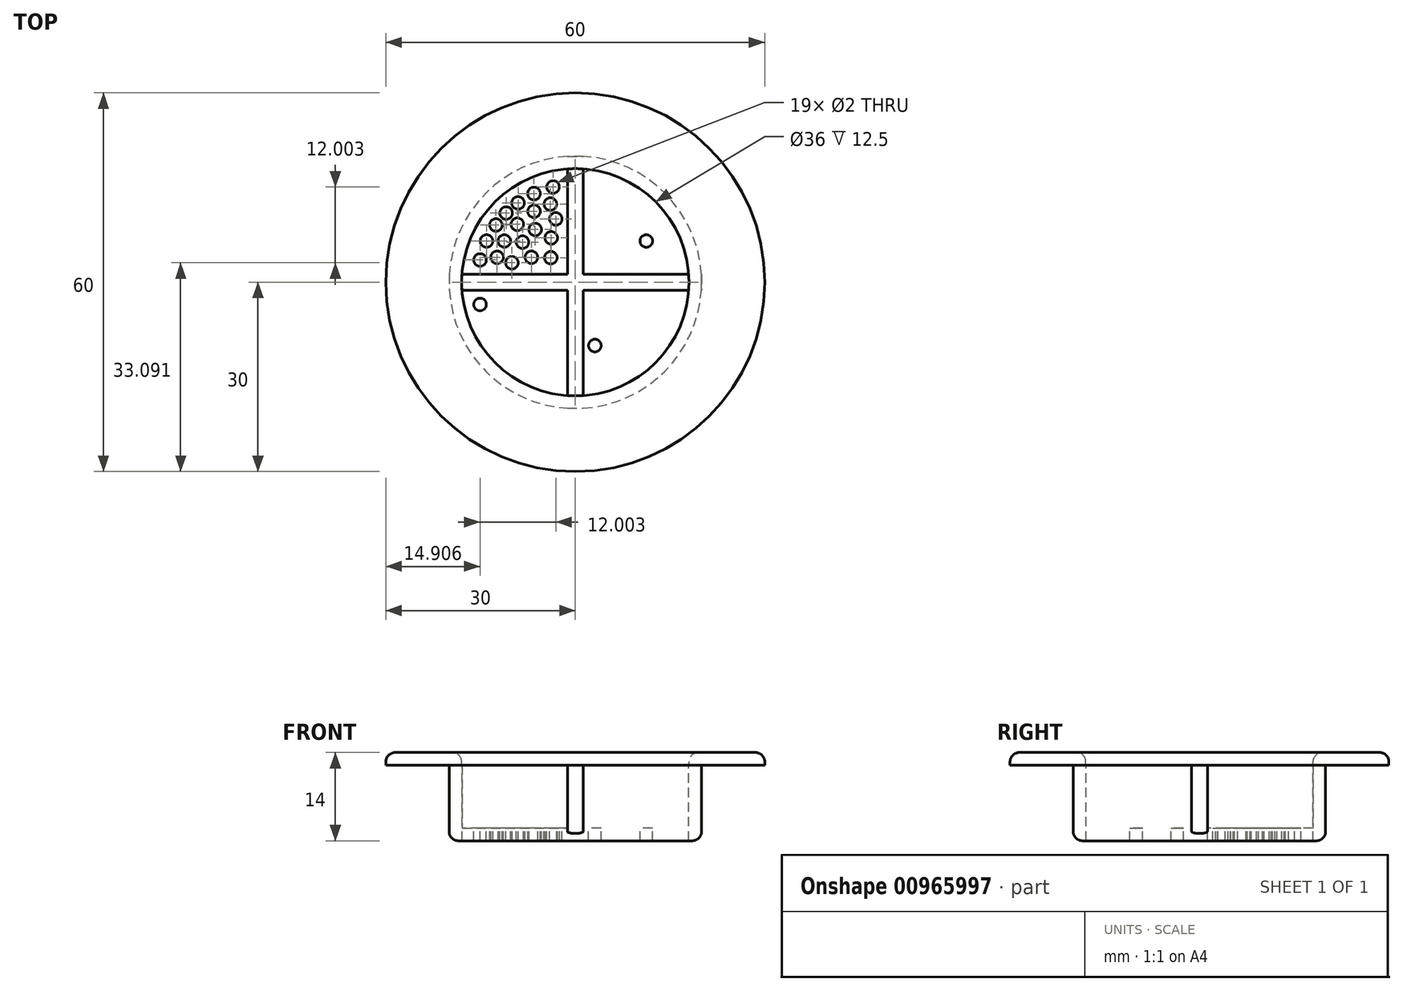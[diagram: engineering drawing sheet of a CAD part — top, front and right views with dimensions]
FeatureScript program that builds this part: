
annotation { "Feature Type Name" : "Feature", "Feature Type Description" : "" }
export const myFeature = defineFeature(function(context is Context, id is Id, definition is map)
    precondition{}
    {
        {
            var Q0;
            Q0=qCreatedBy(makeId("Top.planeOp"),FACE);
            var sketch = newSketch(context, id + "F0", { "sketchPlane" : qUnion([Q0])});
            skCircle(sketch, "E0", {"center": v(0, 0) * mm, "radius": 20 * mm});
            skCircle(sketch, "E1", {"center": v(0, 0) * mm, "radius": 18 * mm});
            skLineSegment(sketch, "E2.bottom", {"start": v(-1.25, 19.96) * mm, "end": v(1.25, 19.96) * mm});
            skLineSegment(sketch, "E2.top", {"start": v(-1.25, -19.96) * mm, "end": v(1.25, -19.96) * mm});
            skLineSegment(sketch, "E2.left", {"start": v(-1.25, 19.96) * mm, "end": v(-1.25, -19.96) * mm});
            skLineSegment(sketch, "E2.right", {"start": v(1.25, 19.96) * mm, "end": v(1.25, -19.96) * mm});
            skLineSegment(sketch, "E3.bottom", {"start": v(-19.96, 1.25) * mm, "end": v(19.96, 1.25) * mm});
            skLineSegment(sketch, "E3.top", {"start": v(-19.96, -1.25) * mm, "end": v(19.96, -1.25) * mm});
            skLineSegment(sketch, "E3.left", {"start": v(-19.96, 1.25) * mm, "end": v(-19.96, -1.25) * mm});
            skLineSegment(sketch, "E3.right", {"start": v(19.96, 1.25) * mm, "end": v(19.96, -1.25) * mm});
            skCircle(sketch, "E4", {"center": v(0, 0) * mm, "radius": 5.5 * mm, "construction": true});
            skCircle(sketch, "E5", {"center": v(0, 0) * mm, "radius": 8 * mm, "construction": true});
            skCircle(sketch, "E6", {"center": v(0, 0) * mm, "radius": 10.5 * mm, "construction": true});
            skCircle(sketch, "E7", {"center": v(0, 0) * mm, "radius": 13 * mm, "construction": true});
            skCircle(sketch, "E8", {"center": v(0, 0) * mm, "radius": 15.5 * mm, "construction": true});
            skLineSegment(sketch, "E9", {"start": v(0, 0) * mm, "end": v(-18.69, 18.69) * mm, "construction": true});
            skCircle(sketch, "E10", {"center": v(-3.89, 3.89) * mm, "radius": 1 * mm});
            skCircle(sketch, "E11", {"center": v(-10.96, 10.96) * mm, "radius": 1 * mm});
            skCircle(sketch, "E12", {"center": v(-6.95, 3.96) * mm, "radius": 1 * mm});
            skCircle(sketch, "E13", {"center": v(-3.81, 7.03) * mm, "radius": 1 * mm});
            skCircle(sketch, "E14", {"center": v(-12.38, 3.96) * mm, "radius": 1 * mm});
            skCircle(sketch, "E15", {"center": v(-15.1, 3.52) * mm, "radius": 1 * mm});
            skCircle(sketch, "E16", {"center": v(-10.03, 3.1) * mm, "radius": 1 * mm});
            skCircle(sketch, "E17", {"center": v(-14.06, 6.53) * mm, "radius": 1 * mm});
            skCircle(sketch, "E18", {"center": v(-11.24, 6.53) * mm, "radius": 1 * mm});
            skCircle(sketch, "E19", {"center": v(-12.57, 9.07) * mm, "radius": 1 * mm});
            skCircle(sketch, "E20", {"center": v(-9.2, 9.2) * mm, "radius": 1 * mm});
            skCircle(sketch, "E21", {"center": v(-8.36, 6.35) * mm, "radius": 1 * mm});
            skCircle(sketch, "E22.MirrorC", {"center": v(-9.07, 12.57) * mm, "radius": 1 * mm});
            skCircle(sketch, "E23.MirrorC", {"center": v(-6.53, 14.06) * mm, "radius": 1 * mm});
            skCircle(sketch, "E24.MirrorC", {"center": v(-3.52, 15.1) * mm, "radius": 1 * mm});
            skCircle(sketch, "E25.MirrorC", {"center": v(-3.96, 12.38) * mm, "radius": 1 * mm});
            skCircle(sketch, "E26.MirrorC", {"center": v(-6.53, 11.24) * mm, "radius": 1 * mm});
            skCircle(sketch, "E27.MirrorC", {"center": v(-3.1, 10.03) * mm, "radius": 1 * mm});
            skCircle(sketch, "E28.MirrorC", {"center": v(-6.35, 8.36) * mm, "radius": 1 * mm});
            skCircle(sketch, "E29.MirrorC", {"center": v(-15.1, -3.52) * mm, "radius": 1 * mm});
            skCircle(sketch, "E30.MirrorC", {"center": v(-12.38, -3.96) * mm, "radius": 1 * mm});
            skCircle(sketch, "E31.MirrorC", {"center": v(-10.03, -3.1) * mm, "radius": 1 * mm});
            skCircle(sketch, "E32.MirrorC", {"center": v(-3.89, -3.89) * mm, "radius": 1 * mm});
            skCircle(sketch, "E33.MirrorC", {"center": v(-3.81, -7.03) * mm, "radius": 1 * mm});
            skCircle(sketch, "E34.MirrorC", {"center": v(-8.36, -6.35) * mm, "radius": 1 * mm});
            skCircle(sketch, "E35.MirrorC", {"center": v(-11.24, -6.53) * mm, "radius": 1 * mm});
            skCircle(sketch, "E36.MirrorC", {"center": v(-14.06, -6.53) * mm, "radius": 1 * mm});
            skCircle(sketch, "E37.MirrorC", {"center": v(-12.57, -9.07) * mm, "radius": 1 * mm});
            skCircle(sketch, "E38.MirrorC", {"center": v(-9.2, -9.2) * mm, "radius": 1 * mm});
            skCircle(sketch, "E39.MirrorC", {"center": v(-10.96, -10.96) * mm, "radius": 1 * mm});
            skCircle(sketch, "E40.MirrorC", {"center": v(-6.35, -8.36) * mm, "radius": 1 * mm});
            skCircle(sketch, "E41.MirrorC", {"center": v(-3.1, -10.03) * mm, "radius": 1 * mm});
            skCircle(sketch, "E42.MirrorC", {"center": v(-3.96, -12.38) * mm, "radius": 1 * mm});
            skCircle(sketch, "E43.MirrorC", {"center": v(-6.53, -11.24) * mm, "radius": 1 * mm});
            skCircle(sketch, "E44.MirrorC", {"center": v(-6.53, -14.06) * mm, "radius": 1 * mm});
            skCircle(sketch, "E45.MirrorC", {"center": v(-9.07, -12.57) * mm, "radius": 1 * mm});
            skCircle(sketch, "E46.MirrorC", {"center": v(-3.52, -15.1) * mm, "radius": 1 * mm});
            skCircle(sketch, "E47.MirrorC", {"center": v(-6.95, -3.96) * mm, "radius": 1 * mm});
            skCircle(sketch, "E48.MirrorC", {"center": v(11.24, 6.53) * mm, "radius": 1 * mm});
            skCircle(sketch, "E49.MirrorC", {"center": v(14.06, 6.53) * mm, "radius": 1 * mm});
            skCircle(sketch, "E50.MirrorC", {"center": v(8.36, 6.35) * mm, "radius": 1 * mm});
            skCircle(sketch, "E51.MirrorC", {"center": v(3.81, 7.03) * mm, "radius": 1 * mm});
            skCircle(sketch, "E52.MirrorC", {"center": v(15.1, 3.52) * mm, "radius": 1 * mm});
            skCircle(sketch, "E53.MirrorC", {"center": v(3.89, 3.89) * mm, "radius": 1 * mm});
            skCircle(sketch, "E54.MirrorC", {"center": v(10.03, 3.1) * mm, "radius": 1 * mm});
            skCircle(sketch, "E55.MirrorC", {"center": v(6.95, 3.96) * mm, "radius": 1 * mm});
            skCircle(sketch, "E56.MirrorC", {"center": v(12.38, 3.96) * mm, "radius": 1 * mm});
            skCircle(sketch, "E57.MirrorC", {"center": v(6.53, 14.06) * mm, "radius": 1 * mm});
            skCircle(sketch, "E58.MirrorC", {"center": v(9.07, 12.57) * mm, "radius": 1 * mm});
            skCircle(sketch, "E59.MirrorC", {"center": v(10.96, 10.96) * mm, "radius": 1 * mm});
            skCircle(sketch, "E60.MirrorC", {"center": v(9.2, 9.2) * mm, "radius": 1 * mm});
            skCircle(sketch, "E61.MirrorC", {"center": v(6.53, 11.24) * mm, "radius": 1 * mm});
            skCircle(sketch, "E62.MirrorC", {"center": v(3.52, 15.1) * mm, "radius": 1 * mm});
            skCircle(sketch, "E63.MirrorC", {"center": v(12.57, 9.07) * mm, "radius": 1 * mm});
            skCircle(sketch, "E64.MirrorC", {"center": v(3.1, 10.03) * mm, "radius": 1 * mm});
            skCircle(sketch, "E65.MirrorC", {"center": v(6.35, 8.36) * mm, "radius": 1 * mm});
            skCircle(sketch, "E66.MirrorC", {"center": v(3.96, 12.38) * mm, "radius": 1 * mm});
            skCircle(sketch, "E67.MirrorC", {"center": v(3.81, -7.03) * mm, "radius": 1 * mm});
            skCircle(sketch, "E68.MirrorC", {"center": v(3.1, -10.03) * mm, "radius": 1 * mm});
            skCircle(sketch, "E69.MirrorC", {"center": v(6.53, -11.24) * mm, "radius": 1 * mm});
            skCircle(sketch, "E70.MirrorC", {"center": v(12.38, -3.96) * mm, "radius": 1 * mm});
            skCircle(sketch, "E71.MirrorC", {"center": v(15.1, -3.52) * mm, "radius": 1 * mm});
            skCircle(sketch, "E72.MirrorC", {"center": v(9.2, -9.2) * mm, "radius": 1 * mm});
            skCircle(sketch, "E73.MirrorC", {"center": v(8.36, -6.35) * mm, "radius": 1 * mm});
            skCircle(sketch, "E74.MirrorC", {"center": v(14.06, -6.53) * mm, "radius": 1 * mm});
            skCircle(sketch, "E75.MirrorC", {"center": v(3.89, -3.89) * mm, "radius": 1 * mm});
            skCircle(sketch, "E76.MirrorC", {"center": v(11.24, -6.53) * mm, "radius": 1 * mm});
            skCircle(sketch, "E77.MirrorC", {"center": v(6.35, -8.36) * mm, "radius": 1 * mm});
            skCircle(sketch, "E78.MirrorC", {"center": v(9.07, -12.57) * mm, "radius": 1 * mm});
            skCircle(sketch, "E79.MirrorC", {"center": v(3.96, -12.38) * mm, "radius": 1 * mm});
            skCircle(sketch, "E80.MirrorC", {"center": v(10.96, -10.96) * mm, "radius": 1 * mm});
            skCircle(sketch, "E81.MirrorC", {"center": v(6.53, -14.06) * mm, "radius": 1 * mm});
            skCircle(sketch, "E82.MirrorC", {"center": v(3.52, -15.1) * mm, "radius": 1 * mm});
            skCircle(sketch, "E83.MirrorC", {"center": v(10.03, -3.1) * mm, "radius": 1 * mm});
            skCircle(sketch, "E84.MirrorC", {"center": v(12.57, -9.07) * mm, "radius": 1 * mm});
            skCircle(sketch, "E85.MirrorC", {"center": v(6.95, -3.96) * mm, "radius": 1 * mm});
            skSolve(sketch);
        }
        {
            var Q0;
            {var subQ0=sQuery(id+"F0.wireOp",EDGE,"E2.left");var subQ5=sQuery(id+"F0.wireOp",EDGE,"E1");var subQ6=makeQuery(id+"F0.imprint","INTERSECT",VERTEX,{"disambiguationData":[OD(0.0)],"derivedFrom":[subQ5,subQ0]});Q0=makeQuery(id+"F0.imprint","IMPRINT",FACE,{"disambiguationData":[TD([[makeQuery(id+"F0.imprint","IMPRINT",EDGE,{"disambiguationData":[TD([[subQ6,-1.0]])],"derivedFrom":subQ5}),-1.0]])]});}
            var Q1;
            Q1=makeQuery(id+"F0.imprint","IMPRINT",FACE,{"disambiguationData":[TD([[makeQuery(id+"F0.imprint","IMPRINT",EDGE,{"derivedFrom":sQuery(id+"F0.wireOp",EDGE,"E10")}),-1.0]])]});
            var Q2;
            {var subQ5=sQuery(id+"F0.wireOp",EDGE,"E3.left");Q2=makeQuery(id+"F0.imprint","IMPRINT",FACE,{"disambiguationData":[TD([[makeQuery(id+"F0.imprint","IMPRINT",EDGE,{"derivedFrom":subQ5}),1.0]])]});}
            var Q3;
            {var subQ0=sQuery(id+"F0.wireOp",EDGE,"E3.bottom");var subQ1=sQuery(id+"F0.wireOp",EDGE,"E1");var subQ2=makeQuery(id+"F0.imprint","INTERSECT",VERTEX,{"disambiguationData":[OD(1.0)],"derivedFrom":[subQ1,subQ0]});Q3=makeQuery(id+"F0.imprint","IMPRINT",FACE,{"disambiguationData":[TD([[makeQuery(id+"F0.imprint","IMPRINT",EDGE,{"disambiguationData":[TD([[subQ2,-1.0]])],"derivedFrom":subQ1}),1.0]])]});}
            var Q4;
            {var subQ3=sQuery(id+"F0.wireOp",EDGE,"E3.top");var subQ5=sQuery(id+"F0.wireOp",EDGE,"E1");var subQ6=makeQuery(id+"F0.imprint","INTERSECT",VERTEX,{"disambiguationData":[OD(0.0)],"derivedFrom":[subQ5,subQ3]});Q4=makeQuery(id+"F0.imprint","IMPRINT",FACE,{"disambiguationData":[TD([[makeQuery(id+"F0.imprint","IMPRINT",EDGE,{"disambiguationData":[TD([[subQ6,-1.0]])],"derivedFrom":subQ5}),-1.0]])]});}
            var Q5;
            Q5=makeQuery(id+"F0.imprint","IMPRINT",FACE,{"disambiguationData":[TD([[makeQuery(id+"F0.imprint","IMPRINT",EDGE,{"derivedFrom":sQuery(id+"F0.wireOp",EDGE,"E29.MirrorC")}),1.0]])]});
            var Q6;
            {var subQ5=sQuery(id+"F0.wireOp",EDGE,"E2.top");Q6=makeQuery(id+"F0.imprint","IMPRINT",FACE,{"disambiguationData":[TD([[makeQuery(id+"F0.imprint","IMPRINT",EDGE,{"derivedFrom":subQ5}),1.0]])]});}
            var Q7;
            {var subQ0=sQuery(id+"F0.wireOp",EDGE,"E2.left");var subQ1=sQuery(id+"F0.wireOp",EDGE,"E1");var subQ2=makeQuery(id+"F0.imprint","INTERSECT",VERTEX,{"disambiguationData":[OD(1.0)],"derivedFrom":[subQ1,subQ0]});Q7=makeQuery(id+"F0.imprint","IMPRINT",FACE,{"disambiguationData":[TD([[makeQuery(id+"F0.imprint","IMPRINT",EDGE,{"disambiguationData":[TD([[subQ2,-1.0]])],"derivedFrom":subQ1}),1.0]])]});}
            var Q8;
            {var subQ0=sQuery(id+"F0.wireOp",EDGE,"E3.bottom");var subQ1=sQuery(id+"F0.wireOp",EDGE,"E2.left");var subQ2=makeQuery(id+"F0.imprint","INTERSECT",VERTEX,{"derivedFrom":[subQ1,subQ0]});Q8=makeQuery(id+"F0.imprint","IMPRINT",FACE,{"disambiguationData":[TD([[makeQuery(id+"F0.imprint","IMPRINT",EDGE,{"disambiguationData":[TD([[subQ2,-1.0]])],"derivedFrom":subQ1}),1.0]])]});}
            var Q9;
            {var subQ0=sQuery(id+"F0.wireOp",EDGE,"E2.right");var subQ1=sQuery(id+"F0.wireOp",EDGE,"E1");var subQ2=makeQuery(id+"F0.imprint","INTERSECT",VERTEX,{"disambiguationData":[OD(0.0)],"derivedFrom":[subQ1,subQ0]});Q9=makeQuery(id+"F0.imprint","IMPRINT",FACE,{"disambiguationData":[TD([[makeQuery(id+"F0.imprint","IMPRINT",EDGE,{"disambiguationData":[TD([[subQ2,-1.0]])],"derivedFrom":subQ1}),1.0]])]});}
            var Q10;
            {var subQ5=sQuery(id+"F0.wireOp",EDGE,"E2.bottom");Q10=makeQuery(id+"F0.imprint","IMPRINT",FACE,{"disambiguationData":[TD([[makeQuery(id+"F0.imprint","IMPRINT",EDGE,{"derivedFrom":subQ5}),-1.0]])]});}
            var Q11;
            {var subQ0=sQuery(id+"F0.wireOp",EDGE,"E2.right");var subQ5=sQuery(id+"F0.wireOp",EDGE,"E1");var subQ6=makeQuery(id+"F0.imprint","INTERSECT",VERTEX,{"disambiguationData":[OD(0.0)],"derivedFrom":[subQ5,subQ0]});Q11=makeQuery(id+"F0.imprint","IMPRINT",FACE,{"disambiguationData":[TD([[makeQuery(id+"F0.imprint","IMPRINT",EDGE,{"disambiguationData":[TD([[subQ6,1.0]])],"derivedFrom":subQ5}),-1.0]])]});}
            var Q12;
            Q12=makeQuery(id+"F0.imprint","IMPRINT",FACE,{"disambiguationData":[TD([[makeQuery(id+"F0.imprint","IMPRINT",EDGE,{"derivedFrom":sQuery(id+"F0.wireOp",EDGE,"E48.MirrorC")}),1.0]])]});
            var Q13;
            {var subQ5=sQuery(id+"F0.wireOp",EDGE,"E3.right");Q13=makeQuery(id+"F0.imprint","IMPRINT",FACE,{"disambiguationData":[TD([[makeQuery(id+"F0.imprint","IMPRINT",EDGE,{"derivedFrom":subQ5}),-1.0]])]});}
            var Q14;
            {var subQ0=sQuery(id+"F0.wireOp",EDGE,"E3.bottom");var subQ1=sQuery(id+"F0.wireOp",EDGE,"E1");var subQ2=makeQuery(id+"F0.imprint","INTERSECT",VERTEX,{"disambiguationData":[OD(0.0)],"derivedFrom":[subQ1,subQ0]});Q14=makeQuery(id+"F0.imprint","IMPRINT",FACE,{"disambiguationData":[TD([[makeQuery(id+"F0.imprint","IMPRINT",EDGE,{"disambiguationData":[TD([[subQ2,1.0]])],"derivedFrom":subQ1}),1.0]])]});}
            var Q15;
            {var subQ0=sQuery(id+"F0.wireOp",EDGE,"E2.right");var subQ5=sQuery(id+"F0.wireOp",EDGE,"E1");var subQ6=makeQuery(id+"F0.imprint","INTERSECT",VERTEX,{"disambiguationData":[OD(1.0)],"derivedFrom":[subQ5,subQ0]});Q15=makeQuery(id+"F0.imprint","IMPRINT",FACE,{"disambiguationData":[TD([[makeQuery(id+"F0.imprint","IMPRINT",EDGE,{"disambiguationData":[TD([[subQ6,-1.0]])],"derivedFrom":subQ5}),-1.0]])]});}
            var Q16;
            Q16=makeQuery(id+"F0.imprint","IMPRINT",FACE,{"disambiguationData":[TD([[makeQuery(id+"F0.imprint","IMPRINT",EDGE,{"derivedFrom":sQuery(id+"F0.wireOp",EDGE,"E68.MirrorC")}),1.0]])]});
            extrude(context, id + "F1", {"entities" : qUnion([Q0, Q1, Q2, Q3, Q4, Q5, Q6, Q7, Q8, Q9, Q10, Q11, Q12, Q13, Q14, Q15, Q16]), "oppositeDirection" : true, "depth" : 2 * mm, "offsetDistance" : 25 * mm});
        }
        {
            var Q0;
            {var subQ0=sQuery(id+"F0.wireOp",EDGE,"E2.left");var subQ5=sQuery(id+"F0.wireOp",EDGE,"E1");var subQ6=makeQuery(id+"F0.imprint","INTERSECT",VERTEX,{"disambiguationData":[OD(0.0)],"derivedFrom":[subQ5,subQ0]});Q0=makeQuery(id+"F0.imprint","IMPRINT",FACE,{"disambiguationData":[TD([[makeQuery(id+"F0.imprint","IMPRINT",EDGE,{"disambiguationData":[TD([[subQ6,-1.0]])],"derivedFrom":subQ5}),-1.0]])]});}
            var Q1;
            {var subQ5=sQuery(id+"F0.wireOp",EDGE,"E3.left");Q1=makeQuery(id+"F0.imprint","IMPRINT",FACE,{"disambiguationData":[TD([[makeQuery(id+"F0.imprint","IMPRINT",EDGE,{"derivedFrom":subQ5}),1.0]])]});}
            var Q2;
            {var subQ5=sQuery(id+"F0.wireOp",EDGE,"E2.bottom");Q2=makeQuery(id+"F0.imprint","IMPRINT",FACE,{"disambiguationData":[TD([[makeQuery(id+"F0.imprint","IMPRINT",EDGE,{"derivedFrom":subQ5}),-1.0]])]});}
            var Q3;
            {var subQ0=sQuery(id+"F0.wireOp",EDGE,"E2.right");var subQ5=sQuery(id+"F0.wireOp",EDGE,"E1");var subQ6=makeQuery(id+"F0.imprint","INTERSECT",VERTEX,{"disambiguationData":[OD(0.0)],"derivedFrom":[subQ5,subQ0]});Q3=makeQuery(id+"F0.imprint","IMPRINT",FACE,{"disambiguationData":[TD([[makeQuery(id+"F0.imprint","IMPRINT",EDGE,{"disambiguationData":[TD([[subQ6,1.0]])],"derivedFrom":subQ5}),-1.0]])]});}
            var Q4;
            {var subQ5=sQuery(id+"F0.wireOp",EDGE,"E3.right");Q4=makeQuery(id+"F0.imprint","IMPRINT",FACE,{"disambiguationData":[TD([[makeQuery(id+"F0.imprint","IMPRINT",EDGE,{"derivedFrom":subQ5}),-1.0]])]});}
            var Q5;
            {var subQ0=sQuery(id+"F0.wireOp",EDGE,"E2.right");var subQ5=sQuery(id+"F0.wireOp",EDGE,"E1");var subQ6=makeQuery(id+"F0.imprint","INTERSECT",VERTEX,{"disambiguationData":[OD(1.0)],"derivedFrom":[subQ5,subQ0]});Q5=makeQuery(id+"F0.imprint","IMPRINT",FACE,{"disambiguationData":[TD([[makeQuery(id+"F0.imprint","IMPRINT",EDGE,{"disambiguationData":[TD([[subQ6,-1.0]])],"derivedFrom":subQ5}),-1.0]])]});}
            var Q6;
            {var subQ5=sQuery(id+"F0.wireOp",EDGE,"E2.top");Q6=makeQuery(id+"F0.imprint","IMPRINT",FACE,{"disambiguationData":[TD([[makeQuery(id+"F0.imprint","IMPRINT",EDGE,{"derivedFrom":subQ5}),1.0]])]});}
            var Q7;
            {var subQ3=sQuery(id+"F0.wireOp",EDGE,"E3.top");var subQ5=sQuery(id+"F0.wireOp",EDGE,"E1");var subQ6=makeQuery(id+"F0.imprint","INTERSECT",VERTEX,{"disambiguationData":[OD(0.0)],"derivedFrom":[subQ5,subQ3]});Q7=makeQuery(id+"F0.imprint","IMPRINT",FACE,{"disambiguationData":[TD([[makeQuery(id+"F0.imprint","IMPRINT",EDGE,{"disambiguationData":[TD([[subQ6,-1.0]])],"derivedFrom":subQ5}),-1.0]])]});}
            extrude(context, id + "F2", {"entities" : qUnion([Q0, Q1, Q2, Q3, Q4, Q5, Q6, Q7]), "operationType" : NewBodyOperationType.ADD, "depth" : 10 * mm, "offsetDistance" : 25 * mm});
        }
        {
            var Q0;
            Q0=makeQuery(id+"F2.opExtrude","CAP_EDGE",EDGE,{"disambiguationData":[OSD([sQuery(id+"F0.wireOp",EDGE,"E1")])],"isStart":true});
            var Q1;
            {var subQ0=sQuery(id+"F0.wireOp",EDGE,"E0");Q1=makeQuery(id+"F1.opExtrude","CAP_EDGE",EDGE,{"disambiguationData":[OSD([subQ0]),TDD([makeQuery(id+"F0.imprint","IMPRINT",EDGE,{"disambiguationData":[TD([[makeQuery(id+"F0.imprint","INTERSECT",VERTEX,{"derivedFrom":[subQ0,sQuery(id+"F0.wireOp",EDGE,"E2.bottom"),sQuery(id+"F0.wireOp",EDGE,"E2.left")]}),-1.0]])],"derivedFrom":subQ0})])],"isStart":false});}
            fillet(context, id + "F3", {"entities" : qUnion([Q0, Q1]), "radius" : 1.5 * mm, "tangentPropagation" : true, "allowEdgeOverflow" : false});
        }
        {
            var Q0;
            Q0=makeQuery(id+"F2.opExtrude","CAP_FACE",FACE,{"disambiguationData":[OSD([sQuery(id+"F0.wireOp",EDGE,"E0"),sQuery(id+"F0.wireOp",EDGE,"E1"),sQuery(id+"F0.wireOp",EDGE,"E2.bottom"),sQuery(id+"F0.wireOp",EDGE,"E2.top"),sQuery(id+"F0.wireOp",EDGE,"E3.left"),sQuery(id+"F0.wireOp",EDGE,"E3.right")])],"isStart":false});
            var sketch = newSketch(context, id + "F4", { "sketchPlane" : qUnion([Q0])});
            skCircle(sketch, "E86.0", {"center": v(0, 0) * mm, "radius": 18 * mm});
            skCircle(sketch, "E87.0", {"center": v(0, 0) * mm, "radius": 30 * mm});
            skSolve(sketch);
        }
        {
            var Q0;
            Q0=makeQuery(id+"F4.imprint","IMPRINT",FACE,{"disambiguationData":[TD([[makeQuery(id+"F4.imprint","IMPRINT",EDGE,{"derivedFrom":sQuery(id+"F4.wireOp",EDGE,"E87.0")}),1.0]])]});
            var Q1;
            Q1=makeQuery(id+"F4.imprint","IMPRINT",FACE,{"disambiguationData":[TD([[makeQuery(id+"F4.imprint","IMPRINT",EDGE,{"derivedFrom":sQuery(id+"F4.wireOp",EDGE,"E86.0")}),-1.0]])]});
            extrude(context, id + "F5", {"entities" : qUnion([Q0, Q1]), "operationType" : NewBodyOperationType.ADD, "depth" : 2 * mm, "offsetDistance" : 25 * mm});
        }
        {
            var Q0;
            Q0=makeQuery(id+"F5.opExtrude","CAP_EDGE",EDGE,{"disambiguationData":[OSD([sQuery(id+"F4.wireOp",EDGE,"E87.0")])],"isStart":false});
            var Q1;
            Q1=makeQuery(id+"F5.opExtrude","CAP_EDGE",EDGE,{"disambiguationData":[OSD([sQuery(id+"F4.wireOp",EDGE,"E86.0")])],"isStart":false});
            fillet(context, id + "F6", {"entities" : qUnion([Q0, Q1]), "radius" : 1.5 * mm, "tangentPropagation" : true, "allowEdgeOverflow" : false});
        }
        {
            var Q0;
            {var subQ0=sQuery(id+"F0.wireOp",EDGE,"E2.left");var subQ1=sQuery(id+"F0.wireOp",EDGE,"E1");var subQ2=makeQuery(id+"F0.imprint","INTERSECT",VERTEX,{"disambiguationData":[OD(1.0)],"derivedFrom":[subQ1,subQ0]});Q0=makeQuery(id+"F0.imprint","IMPRINT",FACE,{"disambiguationData":[TD([[makeQuery(id+"F0.imprint","IMPRINT",EDGE,{"disambiguationData":[TD([[subQ2,-1.0]])],"derivedFrom":subQ1}),1.0]])]});}
            var Q1;
            {var subQ0=sQuery(id+"F0.wireOp",EDGE,"E3.bottom");var subQ1=sQuery(id+"F0.wireOp",EDGE,"E2.left");var subQ2=makeQuery(id+"F0.imprint","INTERSECT",VERTEX,{"derivedFrom":[subQ1,subQ0]});Q1=makeQuery(id+"F0.imprint","IMPRINT",FACE,{"disambiguationData":[TD([[makeQuery(id+"F0.imprint","IMPRINT",EDGE,{"disambiguationData":[TD([[subQ2,-1.0]])],"derivedFrom":subQ1}),1.0]])]});}
            var Q2;
            {var subQ0=sQuery(id+"F0.wireOp",EDGE,"E2.right");var subQ1=sQuery(id+"F0.wireOp",EDGE,"E1");var subQ2=makeQuery(id+"F0.imprint","INTERSECT",VERTEX,{"disambiguationData":[OD(0.0)],"derivedFrom":[subQ1,subQ0]});Q2=makeQuery(id+"F0.imprint","IMPRINT",FACE,{"disambiguationData":[TD([[makeQuery(id+"F0.imprint","IMPRINT",EDGE,{"disambiguationData":[TD([[subQ2,-1.0]])],"derivedFrom":subQ1}),1.0]])]});}
            var Q3;
            {var subQ0=sQuery(id+"F0.wireOp",EDGE,"E3.bottom");var subQ1=sQuery(id+"F0.wireOp",EDGE,"E1");var subQ2=makeQuery(id+"F0.imprint","INTERSECT",VERTEX,{"disambiguationData":[OD(0.0)],"derivedFrom":[subQ1,subQ0]});Q3=makeQuery(id+"F0.imprint","IMPRINT",FACE,{"disambiguationData":[TD([[makeQuery(id+"F0.imprint","IMPRINT",EDGE,{"disambiguationData":[TD([[subQ2,1.0]])],"derivedFrom":subQ1}),1.0]])]});}
            var Q4;
            {var subQ0=sQuery(id+"F0.wireOp",EDGE,"E3.bottom");var subQ1=sQuery(id+"F0.wireOp",EDGE,"E1");var subQ2=makeQuery(id+"F0.imprint","INTERSECT",VERTEX,{"disambiguationData":[OD(1.0)],"derivedFrom":[subQ1,subQ0]});Q4=makeQuery(id+"F0.imprint","IMPRINT",FACE,{"disambiguationData":[TD([[makeQuery(id+"F0.imprint","IMPRINT",EDGE,{"disambiguationData":[TD([[subQ2,-1.0]])],"derivedFrom":subQ1}),1.0]])]});}
            extrude(context, id + "F7", {"entities" : qUnion([Q0, Q1, Q2, Q3, Q4]), "operationType" : NewBodyOperationType.ADD, "depth" : 10 * mm, "offsetDistance" : 25 * mm});
        }
    });
